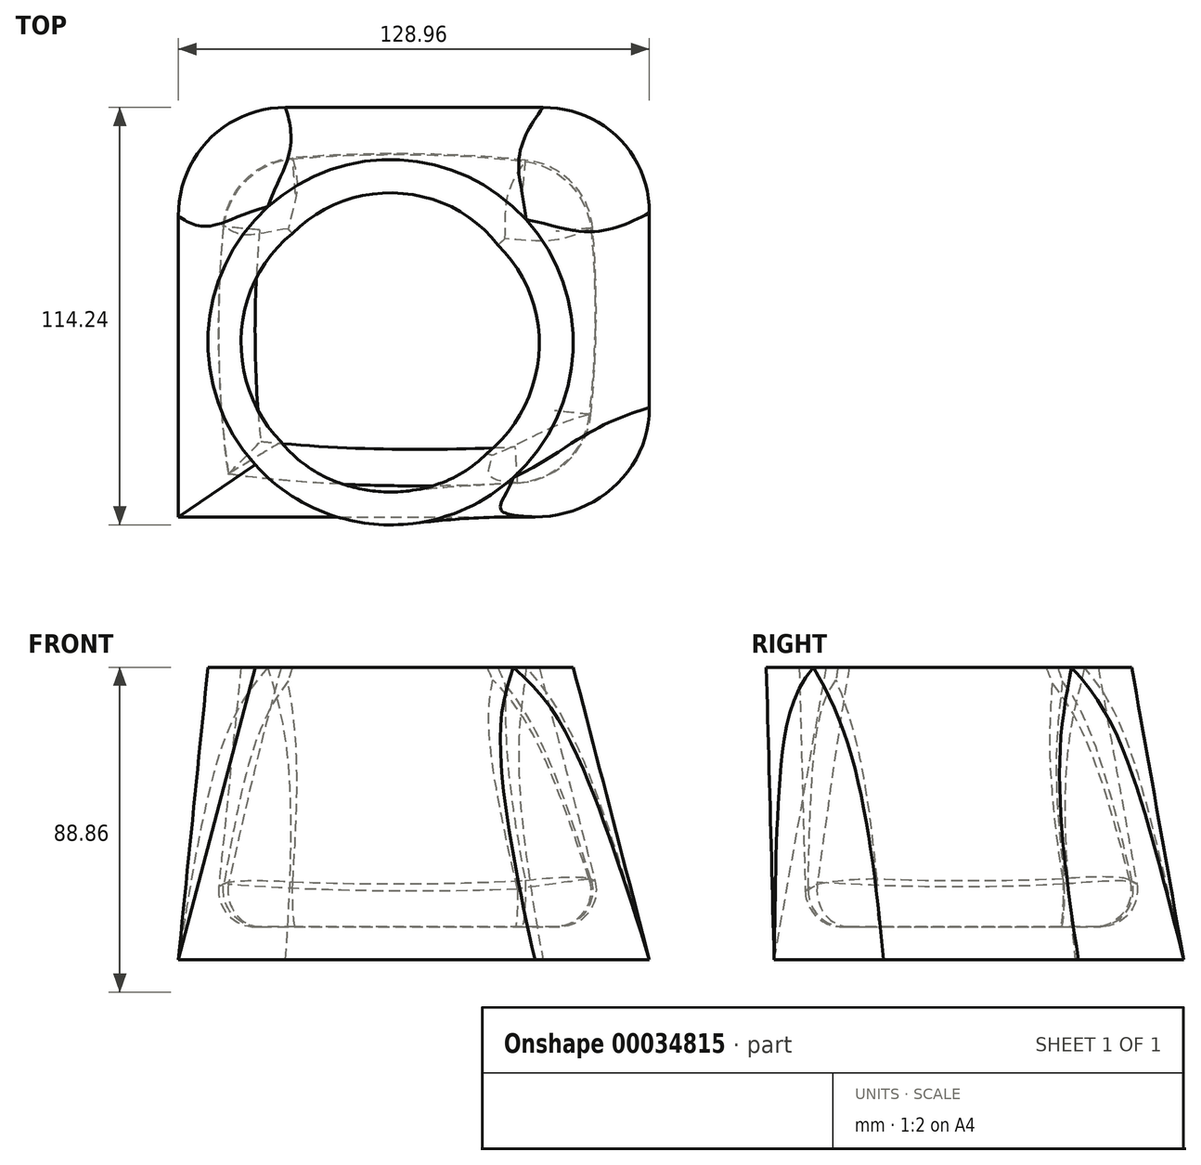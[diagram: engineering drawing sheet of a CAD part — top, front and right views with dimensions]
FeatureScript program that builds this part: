
annotation { "Feature Type Name" : "Feature", "Feature Type Description" : "" }
export const myFeature = defineFeature(function(context is Context, id is Id, definition is map)
    precondition{}
    {
        {
            var Q0;
            Q0=qCreatedBy(makeId("Top.planeOp"),FACE);
            var sketch = newSketch(context, id + "F4", { "sketchPlane" : qUnion([Q0])});
            skLineSegment(sketch, "E0.bottom", {"start": v(-58.11, 64.24) * mm, "end": v(70.85, 64.24) * mm});
            skLineSegment(sketch, "E0.top", {"start": v(-58.11, -47.83) * mm, "end": v(70.85, -47.83) * mm});
            skLineSegment(sketch, "E0.left", {"start": v(-58.11, 64.24) * mm, "end": v(-58.11, -47.83) * mm});
            skLineSegment(sketch, "E0.right", {"start": v(70.85, 64.24) * mm, "end": v(70.85, -47.83) * mm});
            skSolve(sketch);
        }
        {
            var Q0;
            Q0=qCreatedBy(makeId("Top.planeOp"),FACE);
            cPlane(context, id + "F0", {"entities" : qUnion([Q0]), "cplaneType" : CPlaneType.OFFSET, "offset" : 80 * mm, "width" : 152.4 * mm, "height" : 152.4 * mm});
        }
        {
            var Q0;
            Q0=qCreatedBy(id+"F0.planeOp",FACE);
            var sketch = newSketch(context, id + "F1", { "sketchPlane" : qUnion([Q0])});
            skCircle(sketch, "E1", {"center": v(0, 0) * mm, "radius": 50 * mm});
            skSolve(sketch);
        }
        {
            var Q0;
            Q0=qCreatedBy(makeId("Front.planeOp"),FACE);
            var sketch = newSketch(context, id + "F2", { "sketchPlane" : qUnion([Q0])});
            skLineSegment(sketch, "E2.0", {"start": v(-50, 80) * mm, "end": v(50, 80) * mm, "construction": true});
            skLineSegment(sketch, "E3.0", {"start": v(-58.11, 0) * mm, "end": v(70.85, 0) * mm, "construction": true});
            skSolve(sketch);
        }
        {
            var Q0;
            Q0=makeQuery(id+"F4.imprint","IMPRINT",FACE,{"disambiguationData":[TD([[makeQuery(id+"F4.imprint","IMPRINT",EDGE,{"derivedFrom":sQuery(id+"F4.wireOp",EDGE,"E0.bottom")}),-1.0]])]});
            var Q1;
            Q1=makeQuery(id+"F1.imprint","IMPRINT",FACE,{"disambiguationData":[TD([[makeQuery(id+"F1.imprint","IMPRINT",EDGE,{"derivedFrom":sQuery(id+"F1.wireOp",EDGE,"E1")}),1.0]])]});
            loft(context, id + "F5", {"sheetProfilesArray" : [{ "sheetProfileEntities" : qUnion([Q0]) }, { "sheetProfileEntities" : qUnion([Q1]) }]});
        }
        {
            var Q0;
            Q0=makeQuery(id+"F5.opLoft","SWEPT_EDGE",EDGE,{"disambiguationData":[OSD([sQuery(id+"F4.wireOp",EDGE,"E0.top"),sQuery(id+"F4.wireOp",EDGE,"E0.left"),sQuery(id+"F4.wireOp",EDGE,"E0.right"),sQuery(id+"F1.wireOp",EDGE,"E1")])]});
            var Q1;
            Q1=makeQuery(id+"F5.opLoft","SWEPT_EDGE",EDGE,{"disambiguationData":[OSD([sQuery(id+"F4.wireOp",EDGE,"E0.bottom"),sQuery(id+"F4.wireOp",EDGE,"E0.top"),sQuery(id+"F4.wireOp",EDGE,"E0.left"),sQuery(id+"F1.wireOp",EDGE,"E1")])]});
            var Q2;
            Q2=makeQuery(id+"F5.opLoft","SWEPT_EDGE",EDGE,{"disambiguationData":[OSD([sQuery(id+"F4.wireOp",EDGE,"E0.bottom"),sQuery(id+"F4.wireOp",EDGE,"E0.left")])]});
            var Q3;
            Q3=makeQuery(id+"F5.opLoft","SWEPT_EDGE",EDGE,{"disambiguationData":[OSD([sQuery(id+"F4.wireOp",EDGE,"E0.bottom"),sQuery(id+"F4.wireOp",EDGE,"E0.top"),sQuery(id+"F4.wireOp",EDGE,"E0.right"),sQuery(id+"F1.wireOp",EDGE,"E1")])]});
            fillet(context, id + "F6", {"entities" : qUnion([Q0, Q1, Q2, Q3]), "radius" : 30 * mm, "tangentPropagation" : true, "allowEdgeOverflow" : false});
        }
        {
            var Q0;
            Q0=makeQuery(id+"F5.opLoft","CAP_FACE",FACE,{"disambiguationData":[OSD([makeQuery(id+"F1.imprint","IMPRINT",FACE,{"disambiguationData":[TD([[makeQuery(id+"F1.imprint","IMPRINT",EDGE,{"derivedFrom":sQuery(id+"F1.wireOp",EDGE,"E1")}),1.0]])]})])],"isStart":true});
            shell(context, id + "F3", {"entities" : qUnion([Q0]), "thickness" : 9 * mm});
        }
        {
            var Q0;
            Q0=makeQuery(id+"F3.opShell","OFFSET_EDGE",EDGE,{"disambiguationData":[OSD([sQuery(id+"F4.wireOp",EDGE,"E0.bottom"),sQuery(id+"F4.wireOp",EDGE,"E0.left"),sQuery(id+"F4.wireOp",EDGE,"E0.right")])]});
            fillet(context, id + "F7", {"entities" : qUnion([Q0]), "radius" : 10 * mm, "tangentPropagation" : true, "allowEdgeOverflow" : false});
        }
    });
